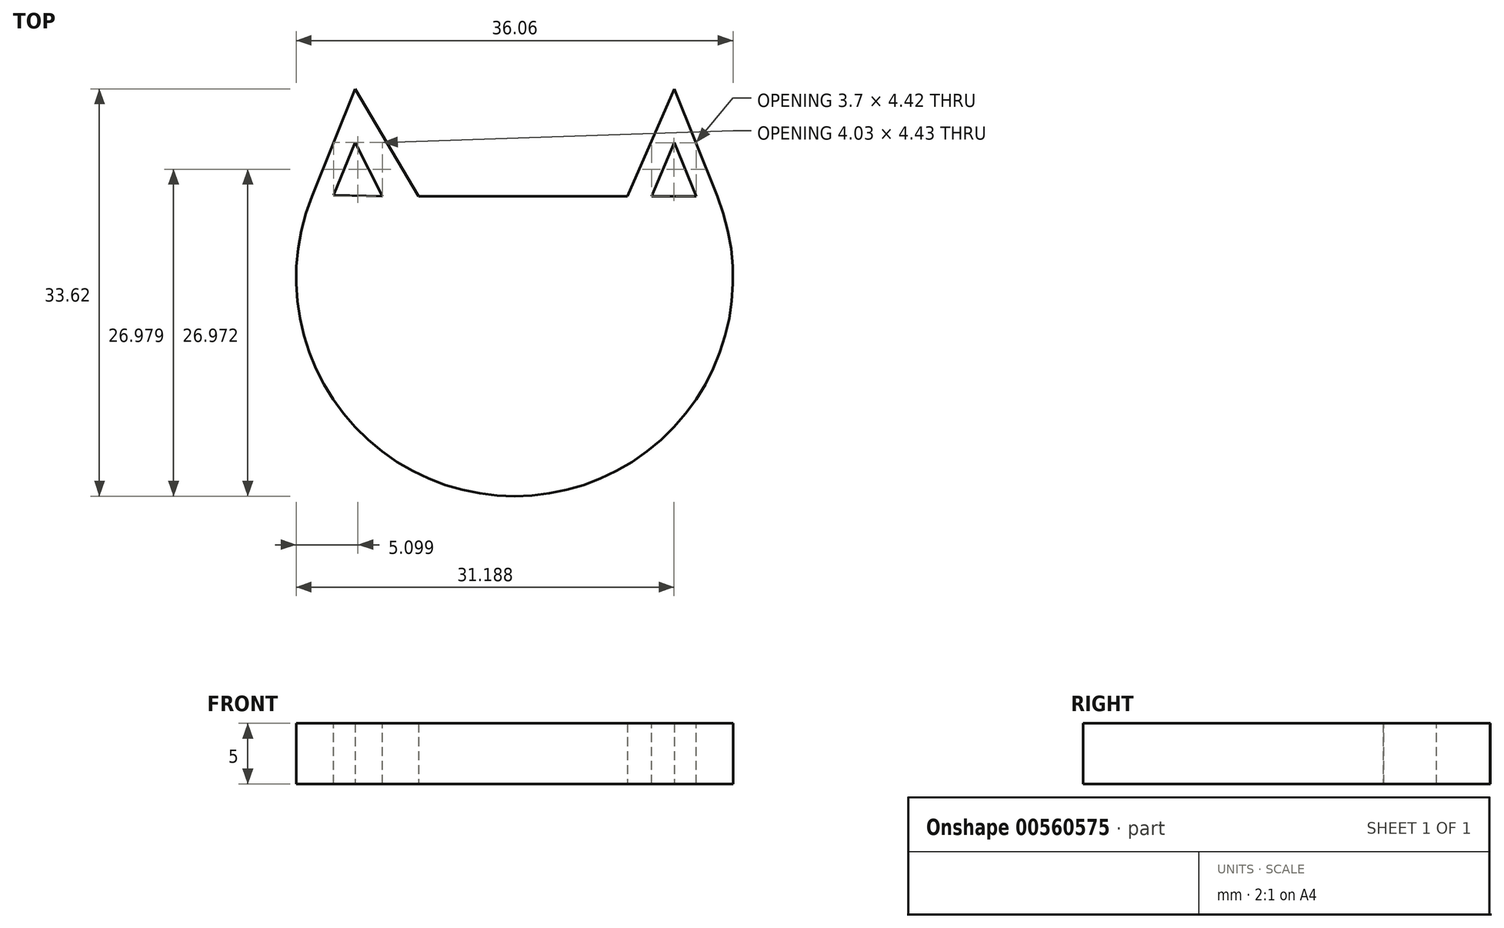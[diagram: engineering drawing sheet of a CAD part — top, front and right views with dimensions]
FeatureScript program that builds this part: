
annotation { "Feature Type Name" : "Feature", "Feature Type Description" : "" }
export const myFeature = defineFeature(function(context is Context, id is Id, definition is map)
    precondition{}
    {
        {
            var Q0;
            Q0=qCreatedBy(makeId("Top.planeOp"),FACE);
            var sketch = newSketch(context, id + "F0", { "sketchPlane" : qUnion([Q0])});
            skArc(sketch, "E0", {"start": v(-16.73, 6.73) * mm, "mid": v(0, -18.03) * mm, "end": v(16.73, 6.73) * mm});
            skLineSegment(sketch, "E1", {"start": v(-7.92, 6.73) * mm, "end": v(9.3, 6.73) * mm});
            skLineSegment(sketch, "E2", {"start": v(-16.73, 6.73) * mm, "end": v(-13.16, 15.6) * mm});
            skLineSegment(sketch, "E3", {"start": v(-13.16, 15.6) * mm, "end": v(-7.92, 6.73) * mm});
            skLineSegment(sketch, "E4", {"start": v(16.73, 6.73) * mm, "end": v(13.17, 15.57) * mm});
            skLineSegment(sketch, "E5", {"start": v(13.17, 15.57) * mm, "end": v(9.3, 6.73) * mm});
            skSolve(sketch);
        }
        {
            var Q0;
            Q0 = qSketchRegion(id + "F0", true);
            extrude(context, id + "F1", {"entities" : qUnion([Q0]), "depth" : 5 * mm, "offsetDistance" : 25 * mm});
        }
        {
            var Q0;
            Q0=makeQuery(id+"F1.opExtrude","CAP_FACE",FACE,{"disambiguationData":[OSD([sQuery(id+"F0.wireOp",EDGE,"E0"),sQuery(id+"F0.wireOp",EDGE,"E1"),sQuery(id+"F0.wireOp",EDGE,"E2"),sQuery(id+"F0.wireOp",EDGE,"E3"),sQuery(id+"F0.wireOp",EDGE,"E4"),sQuery(id+"F0.wireOp",EDGE,"E5")])],"isStart":false});
            var sketch = newSketch(context, id + "F2", { "sketchPlane" : qUnion([Q0])});
            skLineSegment(sketch, "E6", {"start": v(-14.95, 6.82) * mm, "end": v(-10.92, 6.73) * mm});
            skPoint(sketch, "E6.startSnap0", {"position": v(-14.95, 11.16) * mm});
            skLineSegment(sketch, "E7", {"start": v(-10.92, 6.73) * mm, "end": v(-13.16, 11.16) * mm});
            skPoint(sketch, "E7.endSnap0", {"position": v(-10.54, 11.16) * mm});
            skLineSegment(sketch, "E8", {"start": v(-13.16, 11.16) * mm, "end": v(-14.95, 6.82) * mm});
            skSolve(sketch);
        }
        {
            var Q0;
            Q0 = qSketchRegion(id + "F2", true);
            extrude(context, id + "F3", {"entities" : qUnion([Q0]), "operationType" : NewBodyOperationType.REMOVE, "oppositeDirection" : true, "depth" : 15 * mm, "offsetDistance" : 25 * mm});
        }
        {
            var Q0;
            Q0=makeQuery(id+"F1.opExtrude","CAP_FACE",FACE,{"disambiguationData":[OSD([sQuery(id+"F0.wireOp",EDGE,"E0"),sQuery(id+"F0.wireOp",EDGE,"E1"),sQuery(id+"F0.wireOp",EDGE,"E2"),sQuery(id+"F0.wireOp",EDGE,"E3"),sQuery(id+"F0.wireOp",EDGE,"E4"),sQuery(id+"F0.wireOp",EDGE,"E5")])],"isStart":false});
            var sketch = newSketch(context, id + "F4", { "sketchPlane" : qUnion([Q0])});
            skLineSegment(sketch, "E9", {"start": v(11.3, 6.73) * mm, "end": v(15, 6.73) * mm});
            skLineSegment(sketch, "E10", {"start": v(15, 6.73) * mm, "end": v(13.17, 11.15) * mm});
            skPoint(sketch, "E10.endSnap0", {"position": v(11.24, 11.15) * mm});
            skLineSegment(sketch, "E11", {"start": v(13.17, 11.15) * mm, "end": v(11.3, 6.73) * mm});
            skSolve(sketch);
        }
        {
            var Q0;
            Q0 = qSketchRegion(id + "F4", true);
            extrude(context, id + "F5", {"entities" : qUnion([Q0]), "operationType" : NewBodyOperationType.REMOVE, "oppositeDirection" : true, "depth" : 25 * mm, "offsetDistance" : 25 * mm});
        }
    });
